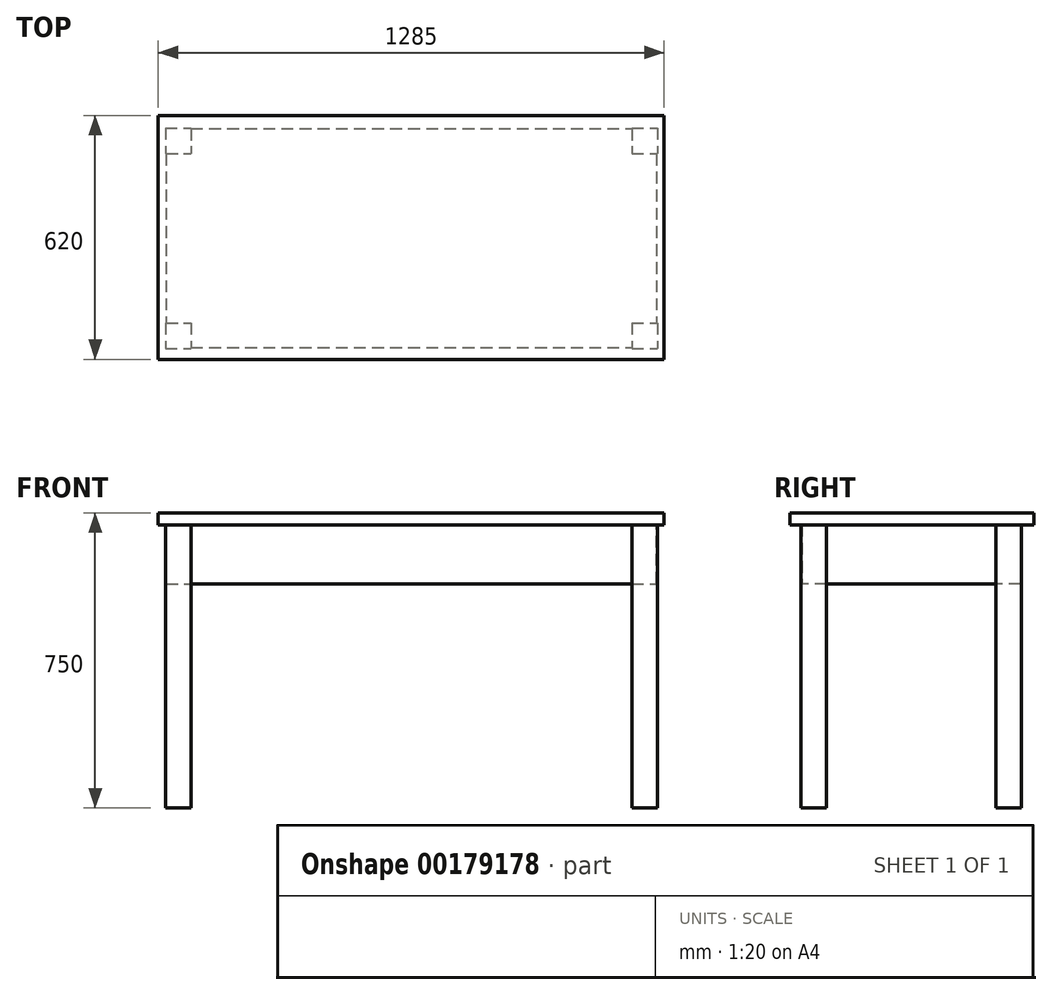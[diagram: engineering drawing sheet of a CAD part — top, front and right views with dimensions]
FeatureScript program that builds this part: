
annotation { "Feature Type Name" : "Feature", "Feature Type Description" : "" }
export const myFeature = defineFeature(function(context is Context, id is Id, definition is map)
    precondition{}
    {
        {
            var Q0;
            Q0=qCreatedBy(makeId("Top.planeOp"),FACE);
            cPlane(context, id + "F0", {"entities" : qUnion([Q0]), "cplaneType" : CPlaneType.OFFSET, "offset" : 720 * mm, "width" : 150 * mm, "height" : 150 * mm});
        }
        {
            var Q0;
            Q0=qCreatedBy(makeId("Top.planeOp"),FACE);
            var sketch = newSketch(context, id + "F1", { "sketchPlane" : qUnion([Q0])});
            skLineSegment(sketch, "E0.bottom", {"start": v(20, 95) * mm, "end": v(85, 95) * mm});
            skLineSegment(sketch, "E0.top", {"start": v(20, 30) * mm, "end": v(85, 30) * mm});
            skLineSegment(sketch, "E0.left", {"start": v(20, 95) * mm, "end": v(20, 30) * mm});
            skLineSegment(sketch, "E0.right", {"start": v(85, 95) * mm, "end": v(85, 30) * mm});
            skLineSegment(sketch, "E1.0.1.0", {"start": v(20, 590) * mm, "end": v(85, 590) * mm});
            skLineSegment(sketch, "E1.0.1.1", {"start": v(20, 525) * mm, "end": v(85, 525) * mm});
            skLineSegment(sketch, "E1.0.1.2", {"start": v(20, 590) * mm, "end": v(20, 525) * mm});
            skLineSegment(sketch, "E1.0.1.3", {"start": v(85, 590) * mm, "end": v(85, 525) * mm});
            skLineSegment(sketch, "E1.1.0.0", {"start": v(1205, 95) * mm, "end": v(1270, 95) * mm});
            skLineSegment(sketch, "E1.1.0.1", {"start": v(1205, 30) * mm, "end": v(1270, 30) * mm});
            skLineSegment(sketch, "E1.1.0.2", {"start": v(1205, 95) * mm, "end": v(1205, 30) * mm});
            skLineSegment(sketch, "E1.1.0.3", {"start": v(1270, 95) * mm, "end": v(1270, 30) * mm});
            skLineSegment(sketch, "E1.1.1.0", {"start": v(1205, 590) * mm, "end": v(1270, 590) * mm});
            skLineSegment(sketch, "E1.1.1.1", {"start": v(1205, 525) * mm, "end": v(1270, 525) * mm});
            skLineSegment(sketch, "E1.1.1.2", {"start": v(1205, 590) * mm, "end": v(1205, 525) * mm});
            skLineSegment(sketch, "E1.1.1.3", {"start": v(1270, 590) * mm, "end": v(1270, 525) * mm});
            skLineSegment(sketch, "E1.direction1", {"start": v(20, 30) * mm, "end": v(1205, 30) * mm, "construction": true});
            skLineSegment(sketch, "E1.direction2", {"start": v(20, 30) * mm, "end": v(20, 525) * mm, "construction": true});
            skSolve(sketch);
        }
        {
            var Q0;
            Q0=makeQuery(id+"F1.imprint","IMPRINT",FACE,{"disambiguationData":[TD([[makeQuery(id+"F1.imprint","IMPRINT",EDGE,{"derivedFrom":sQuery(id+"F1.wireOp",EDGE,"E1.0.1.0")}),-1.0]])]});
            var Q1;
            Q1=makeQuery(id+"F1.imprint","IMPRINT",FACE,{"disambiguationData":[TD([[makeQuery(id+"F1.imprint","IMPRINT",EDGE,{"derivedFrom":sQuery(id+"F1.wireOp",EDGE,"E1.1.0.0")}),-1.0]])]});
            var Q2;
            Q2=makeQuery(id+"F1.imprint","IMPRINT",FACE,{"disambiguationData":[TD([[makeQuery(id+"F1.imprint","IMPRINT",EDGE,{"derivedFrom":sQuery(id+"F1.wireOp",EDGE,"E1.1.1.0")}),-1.0]])]});
            var Q3;
            Q3=makeQuery(id+"F1.imprint","IMPRINT",FACE,{"disambiguationData":[TD([[makeQuery(id+"F1.imprint","IMPRINT",EDGE,{"derivedFrom":sQuery(id+"F1.wireOp",EDGE,"E0.bottom")}),-1.0]])]});
            var Q4;
            Q4=qCreatedBy(id+"F0.planeOp",FACE);
            extrude(context, id + "F2", {"entities" : qUnion([Q0, Q1, Q2, Q3]), "endBound" : BoundingType.UP_TO_SURFACE, "endBoundEntityFace" : qUnion([Q4]), "depth" : 25 * mm});
        }
        {
            var Q0;
            Q0=qCreatedBy(id+"F0.planeOp",FACE);
            var sketch = newSketch(context, id + "F3", { "sketchPlane" : qUnion([Q0])});
            skLineSegment(sketch, "E2.bottom", {"start": v(22, 588) * mm, "end": v(1268, 588) * mm});
            skLineSegment(sketch, "E2.top", {"start": v(22, 32) * mm, "end": v(1268, 32) * mm});
            skLineSegment(sketch, "E2.left", {"start": v(22, 588) * mm, "end": v(22, 32) * mm});
            skLineSegment(sketch, "E2.right", {"start": v(1268, 588) * mm, "end": v(1268, 32) * mm});
            skSolve(sketch);
        }
        {
            var Q0;
            Q0 = qSketchRegion(id + "F3", true);
            extrude(context, id + "F4", {"entities" : qUnion([Q0]), "operationType" : NewBodyOperationType.ADD, "oppositeDirection" : true, "depth" : 150 * mm});
        }
        {
            var Q0;
            Q0=qCreatedBy(id+"F0.planeOp",FACE);
            var sketch = newSketch(context, id + "F5", { "sketchPlane" : qUnion([Q0])});
            skLineSegment(sketch, "E3.bottom", {"start": v(1287, 622) * mm, "end": v(2, 622) * mm});
            skLineSegment(sketch, "E3.top", {"start": v(1287, 2) * mm, "end": v(2, 2) * mm});
            skLineSegment(sketch, "E3.left", {"start": v(1287, 622) * mm, "end": v(1287, 2) * mm});
            skLineSegment(sketch, "E3.right", {"start": v(2, 622) * mm, "end": v(2, 2) * mm});
            skSolve(sketch);
        }
        {
            var Q0;
            Q0 = qSketchRegion(id + "F5", true);
            extrude(context, id + "F6", {"entities" : qUnion([Q0]), "operationType" : NewBodyOperationType.ADD, "depth" : 30 * mm});
        }
    });
